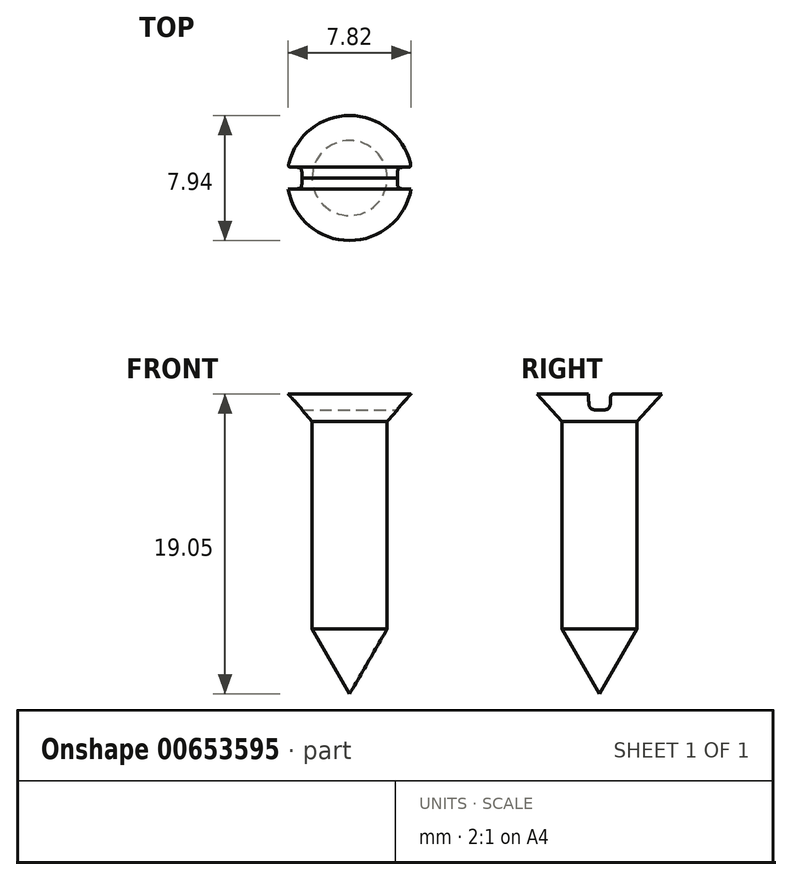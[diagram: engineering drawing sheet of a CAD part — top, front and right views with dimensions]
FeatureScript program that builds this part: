
annotation { "Feature Type Name" : "Feature", "Feature Type Description" : "" }
export const myFeature = defineFeature(function(context is Context, id is Id, definition is map)
    precondition{}
    {
        {
            var Q0;
            Q0=qCreatedBy(makeId("Front.planeOp"),FACE);
            var sketch = newSketch(context, id + "F0", { "sketchPlane" : qUnion([Q0])});
            skLineSegment(sketch, "E0", {"start": v(0, 0) * mm, "end": v(2.38, 4.12) * mm});
            skLineSegment(sketch, "E1", {"start": v(2.38, 4.12) * mm, "end": v(2.38, 17.32) * mm});
            skLineSegment(sketch, "E2", {"start": v(2.38, 17.32) * mm, "end": v(3.97, 19.05) * mm});
            skLineSegment(sketch, "E3", {"start": v(3.97, 19.05) * mm, "end": v(0, 19.05) * mm});
            skLineSegment(sketch, "E4", {"start": v(0, 19.05) * mm, "end": v(0, 0) * mm});
            skLineSegment(sketch, "E5", {"start": v(-2.38, 17.32) * mm, "end": v(-3.97, 19.05) * mm});
            skSolve(sketch);
        }
        {
            var Q0;
            Q0=makeQuery(id+"F0.imprint","IMPRINT",FACE,{"disambiguationData":[TD([[makeQuery(id+"F0.imprint","IMPRINT",EDGE,{"derivedFrom":sQuery(id+"F0.wireOp",EDGE,"E0")}),1.0]])]});
            var Q1;
            Q1=sQuery(id+"F0.wireOp",EDGE,"E4");
            revolve(context, id + "F1", {"entities" : qUnion([Q0]), "axis" : qUnion([Q1]), "revolveType" : RevolveType.FULL});
        }
        {
            var Q0;
            Q0=makeQuery(id+"F1.opRevolve","SWEPT_FACE",FACE,{"disambiguationData":[OSD([sQuery(id+"F0.wireOp",EDGE,"E3")])]});
            var sketch = newSketch(context, id + "F2", { "sketchPlane" : qUnion([Q0])});
            skLineSegment(sketch, "E6.bottom", {"start": v(5.08, 0.7) * mm, "end": v(-5.08, 0.7) * mm});
            skLineSegment(sketch, "E6.top", {"start": v(5.08, -0.7) * mm, "end": v(-5.08, -0.7) * mm});
            skLineSegment(sketch, "E6.left", {"start": v(5.08, 0.7) * mm, "end": v(5.08, -0.7) * mm});
            skLineSegment(sketch, "E6.right", {"start": v(-5.08, 0.7) * mm, "end": v(-5.08, -0.7) * mm});
            skPoint(sketch, "E6.middle", {"position": v(0, 0) * mm});
            skSolve(sketch);
        }
        {
            var Q0;
            {var subQ0=sQuery(id+"F2.wireOp",EDGE,"E6.right");Q0=makeQuery(id+"F2.imprint","IMPRINT",FACE,{"disambiguationData":[TD([[makeQuery(id+"F2.imprint","IMPRINT",EDGE,{"derivedFrom":subQ0}),1.0]])]});}
            var Q1;
            {var subQ0=sQuery(id+"F2.wireOp",EDGE,"E6.bottom");var subQ1=makeQuery(id+"F1.opRevolve","SWEPT_EDGE",EDGE,{"disambiguationData":[OSD([sQuery(id+"F0.wireOp",EDGE,"E2"),sQuery(id+"F0.wireOp",EDGE,"E3")])]});var subQ2=makeQuery(id+"F2.imprint","INTERSECT",VERTEX,{"disambiguationData":[OD(0.0)],"derivedFrom":[subQ1,subQ0]});Q1=makeQuery(id+"F2.imprint","IMPRINT",FACE,{"disambiguationData":[TD([[makeQuery(id+"F2.imprint","IMPRINT",EDGE,{"disambiguationData":[TD([[subQ2,-1.0]])],"derivedFrom":subQ0}),1.0]])]});}
            var Q2;
            {var subQ0=sQuery(id+"F2.wireOp",EDGE,"E6.left");Q2=makeQuery(id+"F2.imprint","IMPRINT",FACE,{"disambiguationData":[TD([[makeQuery(id+"F2.imprint","IMPRINT",EDGE,{"derivedFrom":subQ0}),-1.0]])]});}
            extrude(context, id + "F3", {"entities" : qUnion([Q0, Q1, Q2]), "operationType" : NewBodyOperationType.REMOVE, "oppositeDirection" : true, "depth" : 1.02 * mm, "offsetDistance" : 25.4 * mm});
        }
        {
            var Q0;
            Q0=makeQuery(id+"F3.boolean.opBoolean","COPY",EDGE,{"derivedFrom":makeQuery(id+"F3.opExtrude","CAP_EDGE",EDGE,{"disambiguationData":[OSD([sQuery(id+"F2.wireOp",EDGE,"E6.bottom")])],"isStart":false})});
            var Q1;
            Q1=makeQuery(id+"F3.boolean.opBoolean","COPY",EDGE,{"derivedFrom":makeQuery(id+"F3.opExtrude","CAP_EDGE",EDGE,{"disambiguationData":[OSD([sQuery(id+"F2.wireOp",EDGE,"E6.top")])],"isStart":false})});
            fillet(context, id + "F4", {"entities" : qUnion([Q0, Q1]), "radius" : 0.76 * mm, "tangentPropagation" : true, "rho" : .7, "crossSection" : FilletCrossSection.CONIC, "allowEdgeOverflow" : false});
        }
        {
            var Q0;
            Q0=makeQuery(id+"F3.boolean.opBoolean","COPY",EDGE,{"derivedFrom":makeQuery(id+"F3.opExtrude","CAP_EDGE",EDGE,{"disambiguationData":[OSD([sQuery(id+"F2.wireOp",EDGE,"E6.bottom")])],"isStart":true})});
            var Q1;
            Q1=makeQuery(id+"F3.boolean.opBoolean","COPY",EDGE,{"derivedFrom":makeQuery(id+"F3.opExtrude","CAP_EDGE",EDGE,{"disambiguationData":[OSD([sQuery(id+"F2.wireOp",EDGE,"E6.top")])],"isStart":true})});
            fillet(context, id + "F5", {"entities" : qUnion([Q0, Q1]), "radius" : 0.25 * mm, "tangentPropagation" : true, "rho" : .7, "crossSection" : FilletCrossSection.CONIC, "allowEdgeOverflow" : false});
        }
    });
